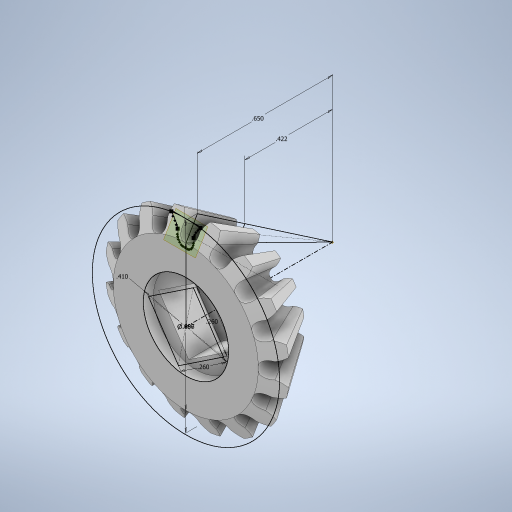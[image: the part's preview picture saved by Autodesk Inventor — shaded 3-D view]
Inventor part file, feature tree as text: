
AUTODESK INVENTOR PART (.ipt)
format: ipt  version: 2023 (Build 270158000, 158)  size: 893,952 bytes
history: native  units: in
note: dims shown in document units (in); Inventor stores cm internally (conversion verified against a paired STEP export)
features: extrude x6, sketch x5, move_body x3, other x2, projected_geometry x2, plane x1, revolve x1, loft x1, boolean_combine x1, pattern_circular x1, chamfer x1
ambient origin geometry x8: Origin, YZ Plane, XZ Plane, XY Plane, X Axis, Y Axis, Z Axis, Center Point
bodies: Solid3 (feature_tree), Solid4 (feature_tree)
feature tree (24):
  extrude  "Extrusion2"  [1 undecoded]
  plane  "Work Plane1"
  move_body  "Move Body1"
  revolve  "Revolution1"  [1 undecoded]
  move_body  "Move Body2"
  move_body  "Move Body3"
  sketch  "Sketch3"  dims[d8=0.697in d9=0.65in]
  other  "Work Point1"
  loft  "Loft1"
  boolean_combine  "Combine1"
  extrude  "Extrusion3"  Depth=0.004in TaperAngle=0.0deg
  pattern_circular  "Circular Pattern1"  [2 undecoded]
  sketch  "Sketch4"  dims[d11=0.422in d14=360.0deg]
  extrude  "Extrusion4"  TaperAngle=0.0deg  [1 undecoded]
  extrude  "Extrusion5"  Depth=0.0586in TaperAngle=0.0deg
  extrude  "Extrusion6"  Depth=6.2992in TaperAngle=360.0deg
  extrude  "Extrusion7"  Depth=0.26in
  chamfer  "Chamfer1"  Distance=0.26in
  sketch  "Sketch2"  dims[d3=0.0039in d4=0.0in d5=-0.2106in]
  projected_geometry  "Projected Loop1"
  other  "Edges1"
  sketch  "Sketch5"  dims[d15=0.2106in d16=0.0in d17=0.004in d18=0.0in]
  sketch  "Sketch6"  dims[d19=0.0in d20=0.0in d21=-0.062in d22=0.886in d23=0.0in d24=90.0deg d25=0.0in d26=90.0deg d27=0.0586in d28=0.0in d29=6.2992in d30=360.0deg d32=0.26in d33=0.26in d34=0.41in d35=0.05in d36=0.0in d37=0.2in d38=0.0in d39=0.13in d40=0.13in d41=0.0in d42=0.0in d43=0.25in d44=0.05in d45=0.0in d46=0.0236in d47=0.125in d48=45.0deg]
  projected_geometry  "Projected Loop2"
note: 5 required parameter values undecoded (feature->parameter linkage not recoverable at this tier; creation-order binding heuristic only, values carry confidence <= 0.55)